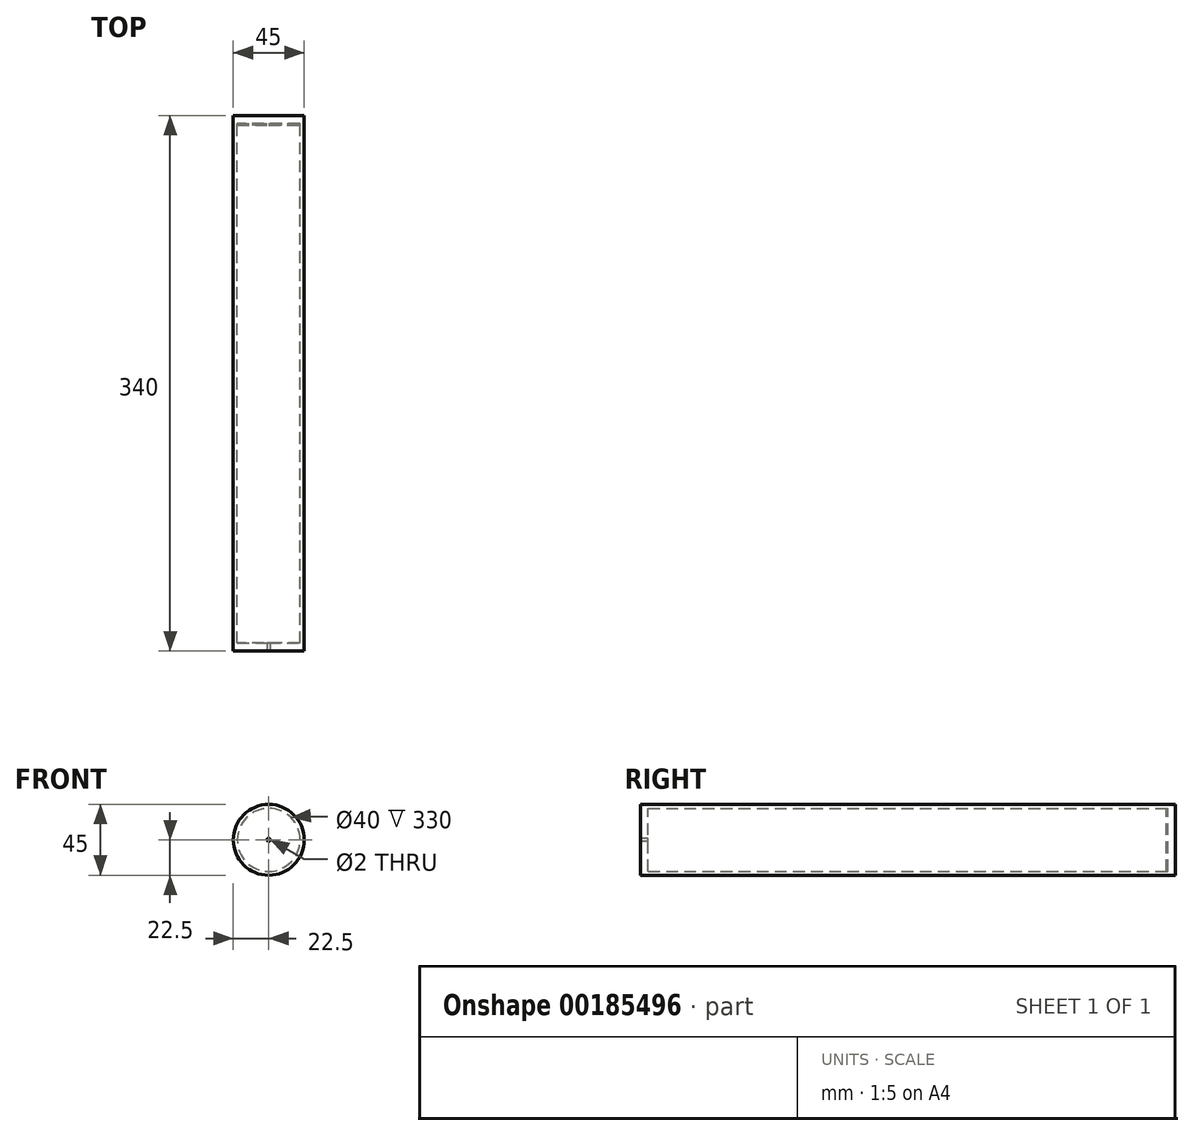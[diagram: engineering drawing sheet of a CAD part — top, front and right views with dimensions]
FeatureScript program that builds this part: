
annotation { "Feature Type Name" : "Feature", "Feature Type Description" : "" }
export const myFeature = defineFeature(function(context is Context, id is Id, definition is map)
    precondition{}
    {
        {
            var Q0;
            Q0=qCreatedBy(makeId("Front.planeOp"),FACE);
            var sketch = newSketch(context, id + "F0", { "sketchPlane" : qUnion([Q0])});
            skCircle(sketch, "E0", {"center": v(0, 0) * mm, "radius": 20 * mm});
            skCircle(sketch, "E1", {"center": v(0, 0) * mm, "radius": 22.5 * mm});
            skCircle(sketch, "E2", {"center": v(0, 0) * mm, "radius": 0.75 * mm});
            skSolve(sketch);
        }
        {
            var Q0;
            Q0 = qSketchRegion(id + "F0", true);
            extrude(context, id + "F1", {"entities" : qUnion([Q0]), "depth" : 330 * mm});
        }
        {
            var Q0;
            Q0=qCreatedBy(makeId("Front.planeOp"),FACE);
            var sketch = newSketch(context, id + "F2", { "sketchPlane" : qUnion([Q0])});
            skCircle(sketch, "E3", {"center": v(0, 0) * mm, "radius": 22.5 * mm});
            skSolve(sketch);
        }
        {
            var Q0;
            Q0 = qSketchRegion(id + "F2", true);
            extrude(context, id + "F3", {"entities" : qUnion([Q0]), "operationType" : NewBodyOperationType.ADD, "oppositeDirection" : true, "depth" : 5 * mm});
        }
        {
            var Q0;
            Q0=makeQuery(id+"F1.opExtrude","CAP_FACE",FACE,{"disambiguationData":[OSD([sQuery(id+"F0.wireOp",EDGE,"E0"),sQuery(id+"F0.wireOp",EDGE,"E1")])],"isStart":false});
            var sketch = newSketch(context, id + "F4", { "sketchPlane" : qUnion([Q0])});
            skCircle(sketch, "E4", {"center": v(0, 0) * mm, "radius": 22.5 * mm});
            skPoint(sketch, "E4.first.point", {"position": v(4.48, 22.05) * mm});
            skPoint(sketch, "E4.second.point", {"position": v(21.2, -7.53) * mm});
            skPoint(sketch, "E4.third.point", {"position": v(-17.2, -14.5) * mm});
            skSolve(sketch);
        }
        {
            var Q0;
            Q0 = qSketchRegion(id + "F4", true);
            extrude(context, id + "F5", {"entities" : qUnion([Q0]), "operationType" : NewBodyOperationType.ADD, "depth" : 5 * mm});
        }
        {
            var Q0;
            Q0=makeQuery(id+"F5.opExtrude","CAP_FACE",FACE,{"disambiguationData":[OSD([sQuery(id+"F4.wireOp",EDGE,"E4")])],"isStart":false});
            var sketch = newSketch(context, id + "F6", { "sketchPlane" : qUnion([Q0])});
            skCircle(sketch, "E5", {"center": v(0, 0) * mm, "radius": 22.5 * mm});
            skPoint(sketch, "E5.first.point", {"position": v(9.2, 20.53) * mm});
            skPoint(sketch, "E5.second.point", {"position": v(16.1, -15.72) * mm});
            skPoint(sketch, "E5.third.point", {"position": v(-22.4, -2.05) * mm});
            skCircle(sketch, "E6", {"center": v(0, 0) * mm, "radius": 1 * mm});
            skSolve(sketch);
        }
        {
            var Q0;
            Q0=makeQuery(id+"F0.imprint","IMPRINT",FACE,{"disambiguationData":[TD([[makeQuery(id+"F0.imprint","IMPRINT",EDGE,{"derivedFrom":sQuery(id+"F0.wireOp",EDGE,"E2")}),1.0]])]});
            var Q1;
            Q1=makeQuery(id+"F0.imprint","IMPRINT",FACE,{"disambiguationData":[TD([[makeQuery(id+"F0.imprint","IMPRINT",EDGE,{"derivedFrom":sQuery(id+"F0.wireOp",EDGE,"E0")}),1.0]])]});
            var Q2;
            Q2=sQuery(id+"F0.wireOp",EDGE,"E0");
            extrude(context, id + "F7", {"entities" : qUnion([Q0, Q1]), "surfaceEntities" : qUnion([Q2]), "depth" : 1 * mm});
        }
        {
            var Q0;
            Q0=makeQuery(id+"F6.imprint","IMPRINT",FACE,{"disambiguationData":[TD([[makeQuery(id+"F6.imprint","IMPRINT",EDGE,{"derivedFrom":sQuery(id+"F6.wireOp",EDGE,"E6")}),1.0]])]});
            extrude(context, id + "F8", {"entities" : qUnion([Q0]), "operationType" : NewBodyOperationType.REMOVE, "oppositeDirection" : true, "depth" : 25 * mm});
        }
    });
